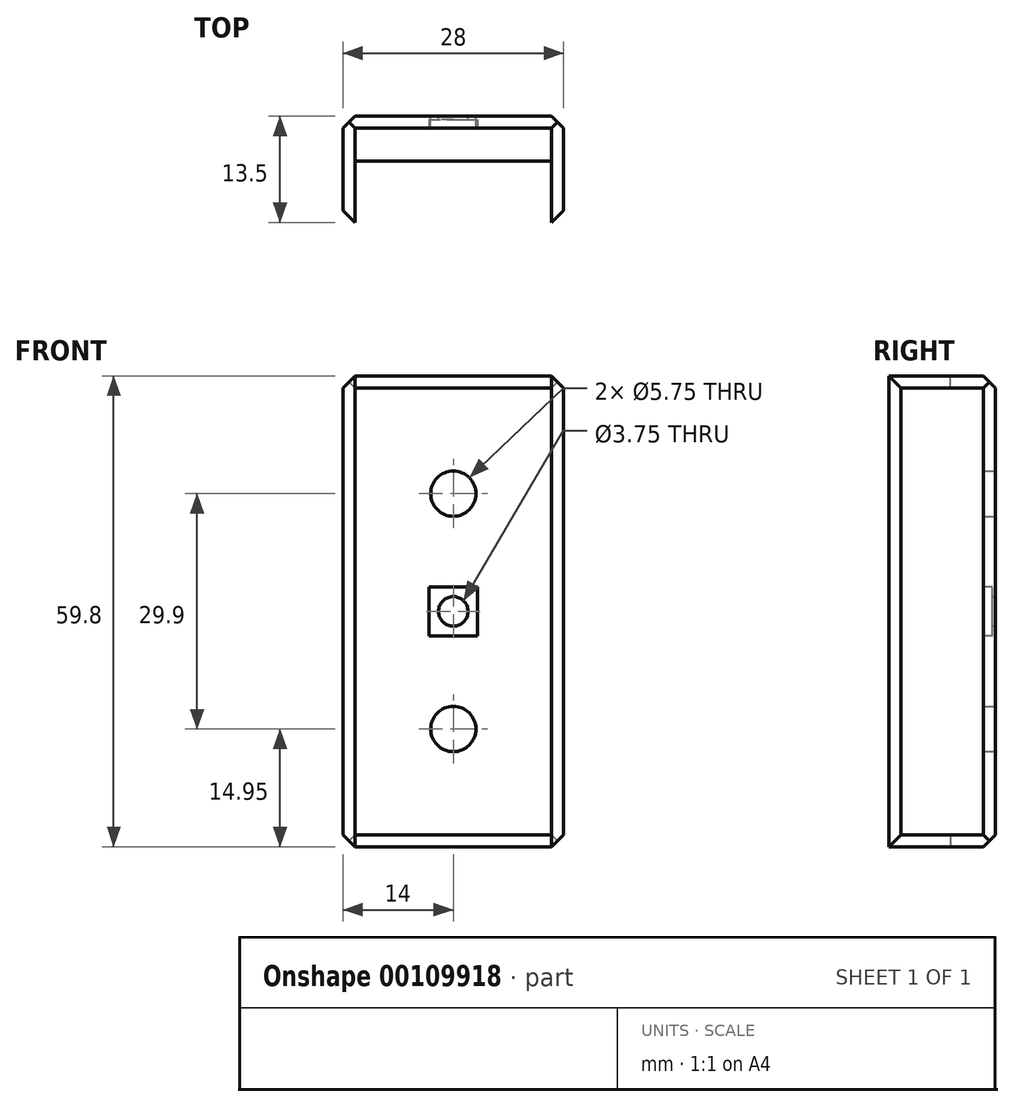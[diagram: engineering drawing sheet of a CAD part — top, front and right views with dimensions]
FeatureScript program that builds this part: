
annotation { "Feature Type Name" : "Feature", "Feature Type Description" : "" }
export const myFeature = defineFeature(function(context is Context, id is Id, definition is map)
    precondition{}
    {
        {
            var Q0;
            Q0=qCreatedBy(makeId("Top.planeOp"),FACE);
            var sketch = newSketch(context, id + "F0", { "sketchPlane" : qUnion([Q0])});
            skLineSegment(sketch, "E0", {"start": v(0, 0) * mm, "end": v(-12.5, 0) * mm});
            skLineSegment(sketch, "E1", {"start": v(-12.5, 0) * mm, "end": v(-12.5, -12) * mm});
            skLineSegment(sketch, "E2", {"start": v(-12.5, -12) * mm, "end": v(-14, -12) * mm});
            skLineSegment(sketch, "E3", {"start": v(-14, -12) * mm, "end": v(-14, 0) * mm});
            skLineSegment(sketch, "E4", {"start": v(-12.5, 1.5) * mm, "end": v(0, 1.5) * mm});
            skLineSegment(sketch, "E5", {"start": v(0, 1.5) * mm, "end": v(0, 0) * mm});
            skLineSegment(sketch, "E6.MirrorCS", {"start": v(12.5, 1.5) * mm, "end": v(0, 1.5) * mm});
            skLineSegment(sketch, "E7.MirrorCS", {"start": v(14, -12) * mm, "end": v(14, 0) * mm});
            skLineSegment(sketch, "E8.MirrorCS", {"start": v(12.5, 0) * mm, "end": v(12.5, -12) * mm});
            skLineSegment(sketch, "E9.MirrorCS", {"start": v(0, 0) * mm, "end": v(12.5, 0) * mm});
            skLineSegment(sketch, "E10.MirrorCS", {"start": v(12.5, -12) * mm, "end": v(14, -12) * mm});
            skLineSegment(sketch, "E11", {"start": v(-14, 0) * mm, "end": v(-14, 1.5) * mm});
            skLineSegment(sketch, "E12", {"start": v(-14, 1.5) * mm, "end": v(-12.5, 1.5) * mm});
            skLineSegment(sketch, "E13", {"start": v(14, 0) * mm, "end": v(14, 1.5) * mm});
            skLineSegment(sketch, "E14", {"start": v(14, 1.5) * mm, "end": v(12.5, 1.5) * mm});
            skSolve(sketch);
        }
        {
            var Q0;
            Q0=makeQuery(id+"F0.imprint","IMPRINT",FACE,{"disambiguationData":[TD([[makeQuery(id+"F0.imprint","IMPRINT",EDGE,{"derivedFrom":sQuery(id+"F0.wireOp",EDGE,"E0")}),-1.0]])]});
            var Q1;
            Q1=makeQuery(id+"F0.imprint","IMPRINT",FACE,{"disambiguationData":[TD([[makeQuery(id+"F0.imprint","IMPRINT",EDGE,{"derivedFrom":sQuery(id+"F0.wireOp",EDGE,"E5")}),1.0]])]});
            extrude(context, id + "F1", {"entities" : qUnion([Q0, Q1]), "depth" : 59.8 * mm});
        }
        {
            var Q0;
            Q0=makeQuery(id+"F1.opExtrude","SWEPT_FACE",FACE,{"disambiguationData":[OSD([sQuery(id+"F0.wireOp",EDGE,"E4"),sQuery(id+"F0.wireOp",EDGE,"E6.MirrorCS")])]});
            var sketch = newSketch(context, id + "F2", { "sketchPlane" : qUnion([Q0])});
            skLineSegment(sketch, "E15", {"start": v(0, 0) * mm, "end": v(0, 59.8) * mm, "construction": true});
            skLineSegment(sketch, "E16", {"start": v(0, 59.8) * mm, "end": v(0, 29.9) * mm, "construction": true});
            skLineSegment(sketch, "E17", {"start": v(0, 29.9) * mm, "end": v(0, 44.85) * mm, "construction": true});
            skLineSegment(sketch, "E18", {"start": v(0, 0) * mm, "end": v(0, 29.9) * mm, "construction": true});
            skLineSegment(sketch, "E19", {"start": v(0, 29.9) * mm, "end": v(0, 14.95) * mm, "construction": true});
            skCircle(sketch, "E20", {"center": v(0, 44.85) * mm, "radius": 2.88 * mm});
            skCircle(sketch, "E21", {"center": v(0, 14.95) * mm, "radius": 2.88 * mm});
            skCircle(sketch, "E22", {"center": v(0, 29.9) * mm, "radius": 1.88 * mm});
            skSolve(sketch);
        }
        {
            var Q0;
            Q0=makeQuery(id+"F2.imprint","IMPRINT",FACE,{"disambiguationData":[TD([[makeQuery(id+"F2.imprint","IMPRINT",EDGE,{"derivedFrom":sQuery(id+"F2.wireOp",EDGE,"E20")}),1.0]])]});
            var Q1;
            Q1=makeQuery(id+"F2.imprint","IMPRINT",FACE,{"disambiguationData":[TD([[makeQuery(id+"F2.imprint","IMPRINT",EDGE,{"derivedFrom":sQuery(id+"F2.wireOp",EDGE,"E22")}),1.0]])]});
            var Q2;
            Q2=makeQuery(id+"F2.imprint","IMPRINT",FACE,{"disambiguationData":[TD([[makeQuery(id+"F2.imprint","IMPRINT",EDGE,{"derivedFrom":sQuery(id+"F2.wireOp",EDGE,"E21")}),1.0]])]});
            extrude(context, id + "F3", {"entities" : qUnion([Q0, Q1, Q2]), "operationType" : NewBodyOperationType.REMOVE, "oppositeDirection" : true, "depth" : 25 * mm});
        }
        {
            var Q0;
            Q0=makeQuery(id+"F1.opExtrude","CAP_FACE",FACE,{"disambiguationData":[OSD([sQuery(id+"F0.wireOp",EDGE,"E0"),sQuery(id+"F0.wireOp",EDGE,"E1"),sQuery(id+"F0.wireOp",EDGE,"E2"),sQuery(id+"F0.wireOp",EDGE,"E3"),sQuery(id+"F0.wireOp",EDGE,"iLumupbO-A0Ql-3wQc-mHnN-mgfWtMwov8ym"),sQuery(id+"F0.wireOp",EDGE,"E4"),sQuery(id+"F0.wireOp",EDGE,"E6.MirrorCS"),sQuery(id+"F0.wireOp",EDGE,"ba8c6c4e-8639-4a23-9431-0b88b56e69950.MirrorCS"),sQuery(id+"F0.wireOp",EDGE,"E7.MirrorCS"),sQuery(id+"F0.wireOp",EDGE,"E8.MirrorCS"),sQuery(id+"F0.wireOp",EDGE,"E9.MirrorCS"),sQuery(id+"F0.wireOp",EDGE,"E10.MirrorCS")])],"isStart":false});
            var sketch = newSketch(context, id + "F4", { "sketchPlane" : qUnion([Q0])});
            skLineSegment(sketch, "E23", {"start": v(-12.5, 0) * mm, "end": v(-12.5, -4.2) * mm});
            skLineSegment(sketch, "E24", {"start": v(-12.5, -4.2) * mm, "end": v(12.5, -4.2) * mm});
            skSolve(sketch);
        }
        {
            var Q0;
            Q0=makeQuery(id+"F4.imprint","IMPRINT",FACE,{"disambiguationData":[TD([[makeQuery(id+"F4.imprint","IMPRINT",EDGE,{"derivedFrom":sQuery(id+"F4.wireOp",EDGE,"E23")}),1.0]])]});
            extrude(context, id + "F5", {"entities" : qUnion([Q0]), "operationType" : NewBodyOperationType.ADD, "oppositeDirection" : true, "depth" : 1.5 * mm});
        }
        {
            var Q0;
            Q0=makeQuery(id+"F1.opExtrude","CAP_FACE",FACE,{"disambiguationData":[OSD([sQuery(id+"F0.wireOp",EDGE,"E0"),sQuery(id+"F0.wireOp",EDGE,"E1"),sQuery(id+"F0.wireOp",EDGE,"E2"),sQuery(id+"F0.wireOp",EDGE,"E3"),sQuery(id+"F0.wireOp",EDGE,"iLumupbO-A0Ql-3wQc-mHnN-mgfWtMwov8ym"),sQuery(id+"F0.wireOp",EDGE,"E4"),sQuery(id+"F0.wireOp",EDGE,"E6.MirrorCS"),sQuery(id+"F0.wireOp",EDGE,"ba8c6c4e-8639-4a23-9431-0b88b56e69950.MirrorCS"),sQuery(id+"F0.wireOp",EDGE,"E7.MirrorCS"),sQuery(id+"F0.wireOp",EDGE,"E8.MirrorCS"),sQuery(id+"F0.wireOp",EDGE,"E9.MirrorCS"),sQuery(id+"F0.wireOp",EDGE,"E10.MirrorCS")])],"isStart":true});
            var sketch = newSketch(context, id + "F6", { "sketchPlane" : qUnion([Q0])});
            skLineSegment(sketch, "E25", {"start": v(-12.5, 0) * mm, "end": v(-12.5, 4.2) * mm});
            skLineSegment(sketch, "E26", {"start": v(-12.5, 4.2) * mm, "end": v(12.5, 4.2) * mm});
            skSolve(sketch);
        }
        {
            var Q0;
            Q0=makeQuery(id+"F6.imprint","IMPRINT",FACE,{"disambiguationData":[TD([[makeQuery(id+"F6.imprint","IMPRINT",EDGE,{"derivedFrom":sQuery(id+"F6.wireOp",EDGE,"E25")}),-1.0]])]});
            extrude(context, id + "F7", {"entities" : qUnion([Q0]), "operationType" : NewBodyOperationType.ADD, "oppositeDirection" : true, "depth" : 1.5 * mm});
        }
        {
            var Q0;
            Q0=makeQuery(id+"F1.opExtrude","SWEPT_EDGE",EDGE,{"disambiguationData":[OSD([sQuery(id+"F0.wireOp",EDGE,"E13"),sQuery(id+"F0.wireOp",EDGE,"E14")])]});
            var Q1;
            Q1=makeQuery(id+"F1.opExtrude","SWEPT_EDGE",EDGE,{"disambiguationData":[OSD([sQuery(id+"F0.wireOp",EDGE,"E11"),sQuery(id+"F0.wireOp",EDGE,"E12")])]});
            var Q2;
            Q2=makeQuery(id+"F1.opExtrude","CAP_EDGE",EDGE,{"disambiguationData":[OSD([sQuery(id+"F0.wireOp",EDGE,"E4"),sQuery(id+"F0.wireOp",EDGE,"E6.MirrorCS"),sQuery(id+"F0.wireOp",EDGE,"E12"),sQuery(id+"F0.wireOp",EDGE,"E14")])],"isStart":true});
            var Q3;
            Q3=makeQuery(id+"F1.opExtrude","CAP_EDGE",EDGE,{"disambiguationData":[OSD([sQuery(id+"F0.wireOp",EDGE,"E4"),sQuery(id+"F0.wireOp",EDGE,"E6.MirrorCS"),sQuery(id+"F0.wireOp",EDGE,"E12"),sQuery(id+"F0.wireOp",EDGE,"E14")])],"isStart":false});
            chamfer(context, id + "F8", {"entities" : qUnion([Q0, Q1, Q2, Q3]), "width" : 1.5 * mm, "tangentPropagation" : true});
        }
        {
            var Q0;
            Q0=makeQuery(id+"F1.opExtrude","CAP_EDGE",EDGE,{"disambiguationData":[OSD([sQuery(id+"F0.wireOp",EDGE,"E3"),sQuery(id+"F0.wireOp",EDGE,"E11")])],"isStart":true});
            var Q1;
            Q1=makeQuery(id+"F1.opExtrude","CAP_EDGE",EDGE,{"disambiguationData":[OSD([sQuery(id+"F0.wireOp",EDGE,"E7.MirrorCS"),sQuery(id+"F0.wireOp",EDGE,"E13")])],"isStart":true});
            var Q2;
            Q2=makeQuery(id+"F1.opExtrude","CAP_EDGE",EDGE,{"disambiguationData":[OSD([sQuery(id+"F0.wireOp",EDGE,"E3"),sQuery(id+"F0.wireOp",EDGE,"E11")])],"isStart":false});
            var Q3;
            Q3=makeQuery(id+"F1.opExtrude","CAP_EDGE",EDGE,{"disambiguationData":[OSD([sQuery(id+"F0.wireOp",EDGE,"E7.MirrorCS"),sQuery(id+"F0.wireOp",EDGE,"E13")])],"isStart":false});
            chamfer(context, id + "F9", {"entities" : qUnion([Q0, Q1, Q2, Q3]), "width" : 1.5 * mm, "tangentPropagation" : true});
        }
        {
            var Q0;
            Q0=makeQuery(id+"F1.opExtrude","SWEPT_FACE",FACE,{"disambiguationData":[OSD([sQuery(id+"F0.wireOp",EDGE,"E0"),sQuery(id+"F0.wireOp",EDGE,"E9.MirrorCS")])]});
            var sketch = newSketch(context, id + "F10", { "sketchPlane" : qUnion([Q0])});
            skLineSegment(sketch, "E27", {"start": v(0, 29.9) * mm, "end": v(0, 33) * mm});
            skLineSegment(sketch, "E28", {"start": v(0, 33) * mm, "end": v(3.1, 33) * mm});
            skLineSegment(sketch, "E29", {"start": v(3.1, 33) * mm, "end": v(3.1, 29.9) * mm});
            skLineSegment(sketch, "E30", {"start": v(3.1, 29.9) * mm, "end": v(3.1, 26.8) * mm});
            skLineSegment(sketch, "E31", {"start": v(3.1, 26.8) * mm, "end": v(0, 26.8) * mm});
            skLineSegment(sketch, "E32", {"start": v(0, 26.8) * mm, "end": v(-3.1, 26.8) * mm});
            skLineSegment(sketch, "E33", {"start": v(-3.1, 26.8) * mm, "end": v(-3.1, 33) * mm});
            skLineSegment(sketch, "E34", {"start": v(0, 33) * mm, "end": v(-3.1, 33) * mm});
            skSolve(sketch);
        }
        {
            var Q0;
            Q0 = qSketchRegion(id + "F10", true);
            extrude(context, id + "F11", {"entities" : qUnion([Q0]), "operationType" : NewBodyOperationType.REMOVE, "oppositeDirection" : true, "depth" : 1.1 * mm});
        }
        {
            var Q0;
            Q0=makeQuery(id+"F1.opExtrude","SWEPT_EDGE",EDGE,{"disambiguationData":[OSD([sQuery(id+"F0.wireOp",EDGE,"E2"),sQuery(id+"F0.wireOp",EDGE,"E3")])]});
            var Q1;
            Q1=makeQuery(id+"F1.opExtrude","SWEPT_EDGE",EDGE,{"disambiguationData":[OSD([sQuery(id+"F0.wireOp",EDGE,"E7.MirrorCS"),sQuery(id+"F0.wireOp",EDGE,"E10.MirrorCS")])]});
            chamfer(context, id + "F12", {"entities" : qUnion([Q0, Q1]), "width" : 1.5 * mm, "tangentPropagation" : true});
        }
    });
